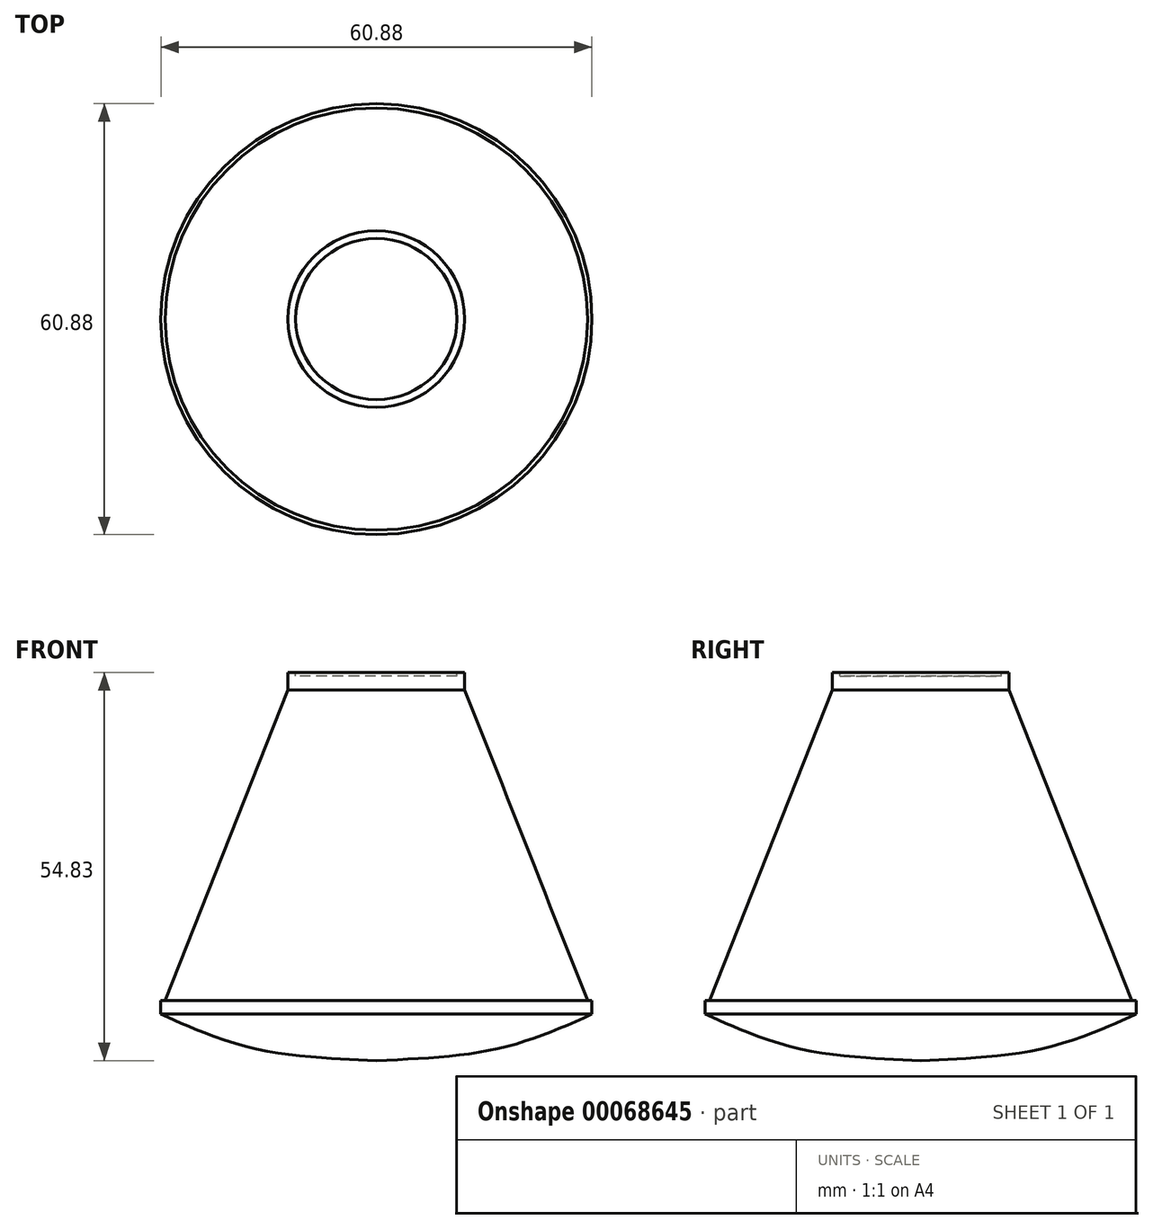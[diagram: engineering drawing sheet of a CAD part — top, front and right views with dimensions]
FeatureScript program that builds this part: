
annotation { "Feature Type Name" : "Feature", "Feature Type Description" : "" }
export const myFeature = defineFeature(function(context is Context, id is Id, definition is map)
    precondition{}
    {
        {
            var Q0;
            Q0=qCreatedBy(makeId("Front.planeOp"),FACE);
            var sketch = newSketch(context, id + "F0", { "sketchPlane" : qUnion([Q0])});
            skLineSegment(sketch, "E0", {"start": v(0, 47.8) * mm, "end": v(0, -6.55) * mm});
            skFitSpline(sketch, "E1", {"points": [v(0, -6.55) * mm, v(17.33, -4.82) * mm, v(30.44, 0) * mm], "startDerivative": vector(34.2, 1.45) * mm, "endDerivative": vector(26.54, 11.85) * mm});
            skLineSegment(sketch, "E2", {"start": v(30.44, 0) * mm, "end": v(30.44, 1.94) * mm});
            skLineSegment(sketch, "E3", {"start": v(30.44, 1.94) * mm, "end": v(29.82, 1.94) * mm});
            skLineSegment(sketch, "E4", {"start": v(29.82, 1.94) * mm, "end": v(12.47, 45.82) * mm});
            skLineSegment(sketch, "E5", {"start": v(12.47, 45.82) * mm, "end": v(12.47, 48.28) * mm});
            skLineSegment(sketch, "E6", {"start": v(12.47, 48.28) * mm, "end": v(11.4, 48.28) * mm});
            skLineSegment(sketch, "E7", {"start": v(11.4, 48.28) * mm, "end": v(11.4, 47.8) * mm});
            skLineSegment(sketch, "E8", {"start": v(11.4, 47.8) * mm, "end": v(0, 47.8) * mm});
            skSolve(sketch);
        }
        {
            var Q0;
            Q0 = qSketchRegion(id + "F0", true);
            var Q1;
            Q1=sQuery(id+"F0.wireOp",EDGE,"E0");
            revolve(context, id + "F1", {"entities" : qUnion([Q0]), "axis" : qUnion([Q1]), "revolveType" : RevolveType.FULL});
        }
        {
            var Q0;
            Q0=qCreatedBy(makeId("Front.planeOp"),FACE);
            var sketch = newSketch(context, id + "F2", { "sketchPlane" : qUnion([Q0])});
            skLineSegment(sketch, "E9", {"start": v(-21.98, 12.01) * mm, "end": v(0, 12.01) * mm});
            skLineSegment(sketch, "E10", {"start": v(0, 45.27) * mm, "end": v(-10.21, 45.23) * mm});
            skLineSegment(sketch, "E11", {"start": v(-10.21, 45.23) * mm, "end": v(-21.98, 12.01) * mm});
            skLineSegment(sketch, "E12.MirrorCS", {"start": v(22.3, 12.22) * mm, "end": v(0, 12.01) * mm});
            skLineSegment(sketch, "E13.MirrorCS", {"start": v(10.21, 45.32) * mm, "end": v(22.3, 12.22) * mm});
            skLineSegment(sketch, "E14.MirrorCS", {"start": v(0, 45.27) * mm, "end": v(10.21, 45.32) * mm});
            skSolve(sketch);
        }
        {
            var Q0;
            Q0 = qSketchRegion(id + "F2", true);
            extrude(context, id + "F3", {"entities" : qUnion([Q0]), "operationType" : NewBodyOperationType.ADD, "endBound" : BoundingType.UP_TO_NEXT, "depth" : 25.4 * mm});
        }
    });
